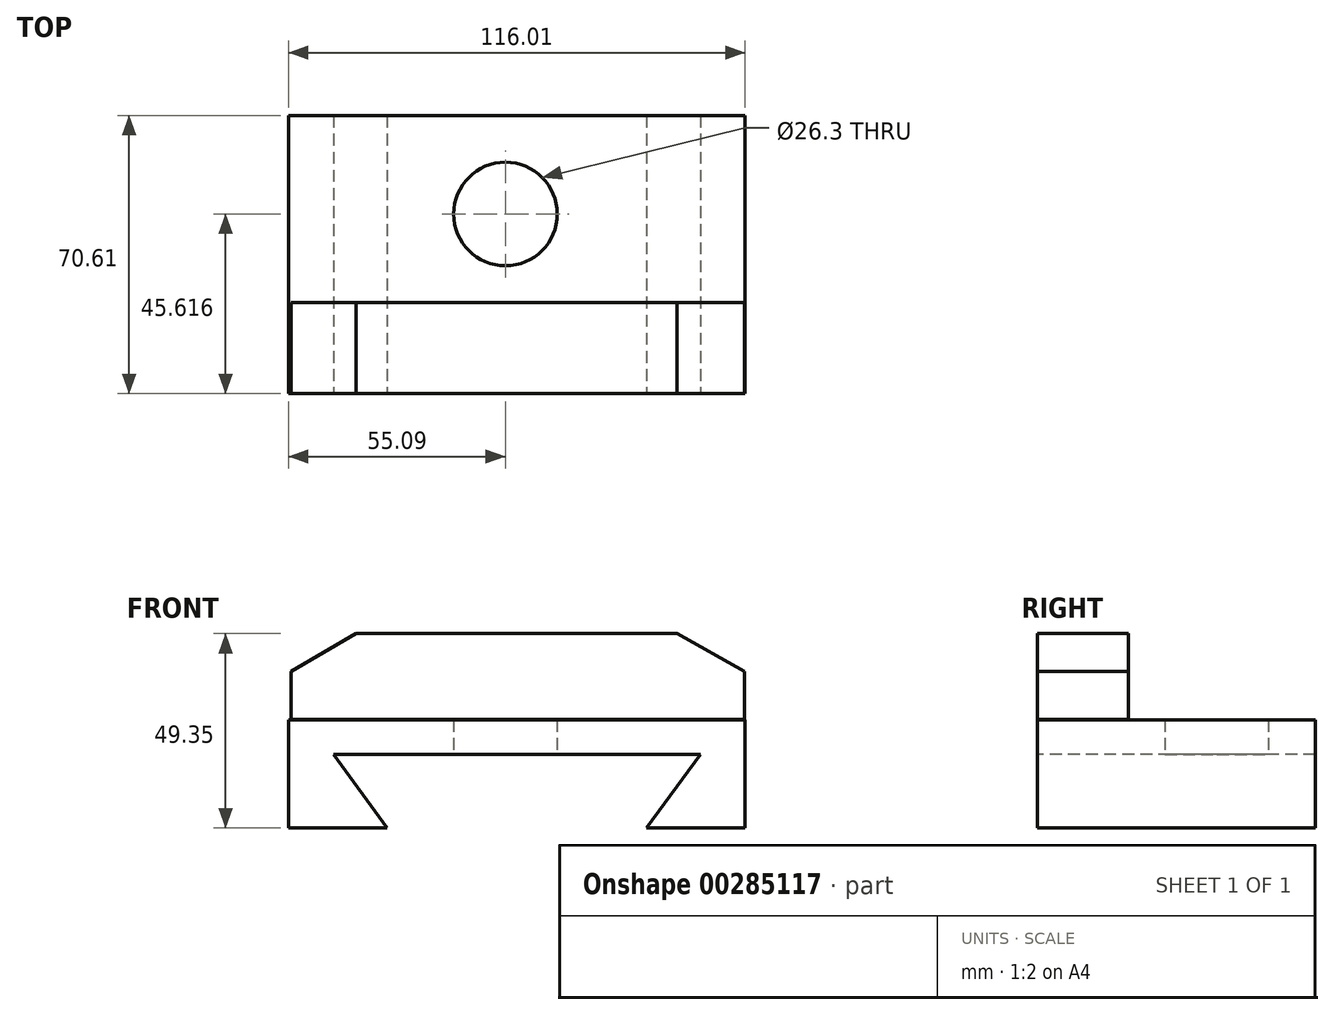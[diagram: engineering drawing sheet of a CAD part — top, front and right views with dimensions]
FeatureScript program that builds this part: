
annotation { "Feature Type Name" : "Feature", "Feature Type Description" : "" }
export const myFeature = defineFeature(function(context is Context, id is Id, definition is map)
    precondition{}
    {
        {
            var Q0;
            Q0=qCreatedBy(makeId("Front.planeOp"),FACE);
            var sketch = newSketch(context, id + "F0", { "sketchPlane" : qUnion([Q0])});
            skLineSegment(sketch, "E0", {"start": v(-55.09, 15.89) * mm, "end": v(-55.09, -11.51) * mm});
            skLineSegment(sketch, "E1", {"start": v(-55.09, -11.51) * mm, "end": v(-30.02, -11.51) * mm});
            skLineSegment(sketch, "E2", {"start": v(-30.02, -11.51) * mm, "end": v(-43.72, 7.14) * mm});
            skLineSegment(sketch, "E3", {"start": v(-43.72, 7.14) * mm, "end": v(49.55, 7.14) * mm});
            skLineSegment(sketch, "E4", {"start": v(49.55, 7.14) * mm, "end": v(35.85, -11.51) * mm});
            skLineSegment(sketch, "E5", {"start": v(35.85, -11.51) * mm, "end": v(60.92, -11.51) * mm});
            skLineSegment(sketch, "E6", {"start": v(60.92, -11.51) * mm, "end": v(60.92, 15.89) * mm});
            skLineSegment(sketch, "E7", {"start": v(60.92, 15.89) * mm, "end": v(-55.09, 15.89) * mm});
            skSolve(sketch);
        }
        {
            var Q0;
            Q0 = qSketchRegion(id + "F0", true);
            extrude(context, id + "F1", {"entities" : qUnion([Q0]), "oppositeDirection" : true, "depth" : 70.61 * mm});
        }
        {
            var Q0;
            Q0=qCreatedBy(makeId("Front.planeOp"),FACE);
            var sketch = newSketch(context, id + "F2", { "sketchPlane" : qUnion([Q0])});
            skLineSegment(sketch, "E8", {"start": v(60.71, 16.07) * mm, "end": v(60.71, 28.2) * mm});
            skLineSegment(sketch, "E9", {"start": v(-54.5, 16.07) * mm, "end": v(-54.5, 28.2) * mm});
            skLineSegment(sketch, "E10", {"start": v(-54.5, 28.2) * mm, "end": v(-37.97, 37.84) * mm});
            skLineSegment(sketch, "E11", {"start": v(-37.97, 37.84) * mm, "end": v(43.62, 37.84) * mm});
            skLineSegment(sketch, "E12", {"start": v(60.71, 16.07) * mm, "end": v(-54.5, 16.07) * mm});
            skLineSegment(sketch, "E13", {"start": v(43.62, 37.84) * mm, "end": v(60.71, 28.2) * mm});
            skSolve(sketch);
        }
        {
            var Q0;
            Q0 = qSketchRegion(id + "F2", true);
            extrude(context, id + "F3", {"entities" : qUnion([Q0]), "oppositeDirection" : true, "depth" : 23.1 * mm});
        }
        {
            var Q0;
            Q0=qCreatedBy(makeId("Top.planeOp"),FACE);
            var sketch = newSketch(context, id + "F4", { "sketchPlane" : qUnion([Q0])});
            skCircle(sketch, "E14", {"center": v(0, 45.62) * mm, "radius": 13.15 * mm});
            skSolve(sketch);
        }
        {
            var Q0;
            Q0 = qSketchRegion(id + "F4", true);
            extrude(context, id + "F5", {"entities" : qUnion([Q0]), "operationType" : NewBodyOperationType.REMOVE, "depth" : 25.4 * mm});
        }
    });
